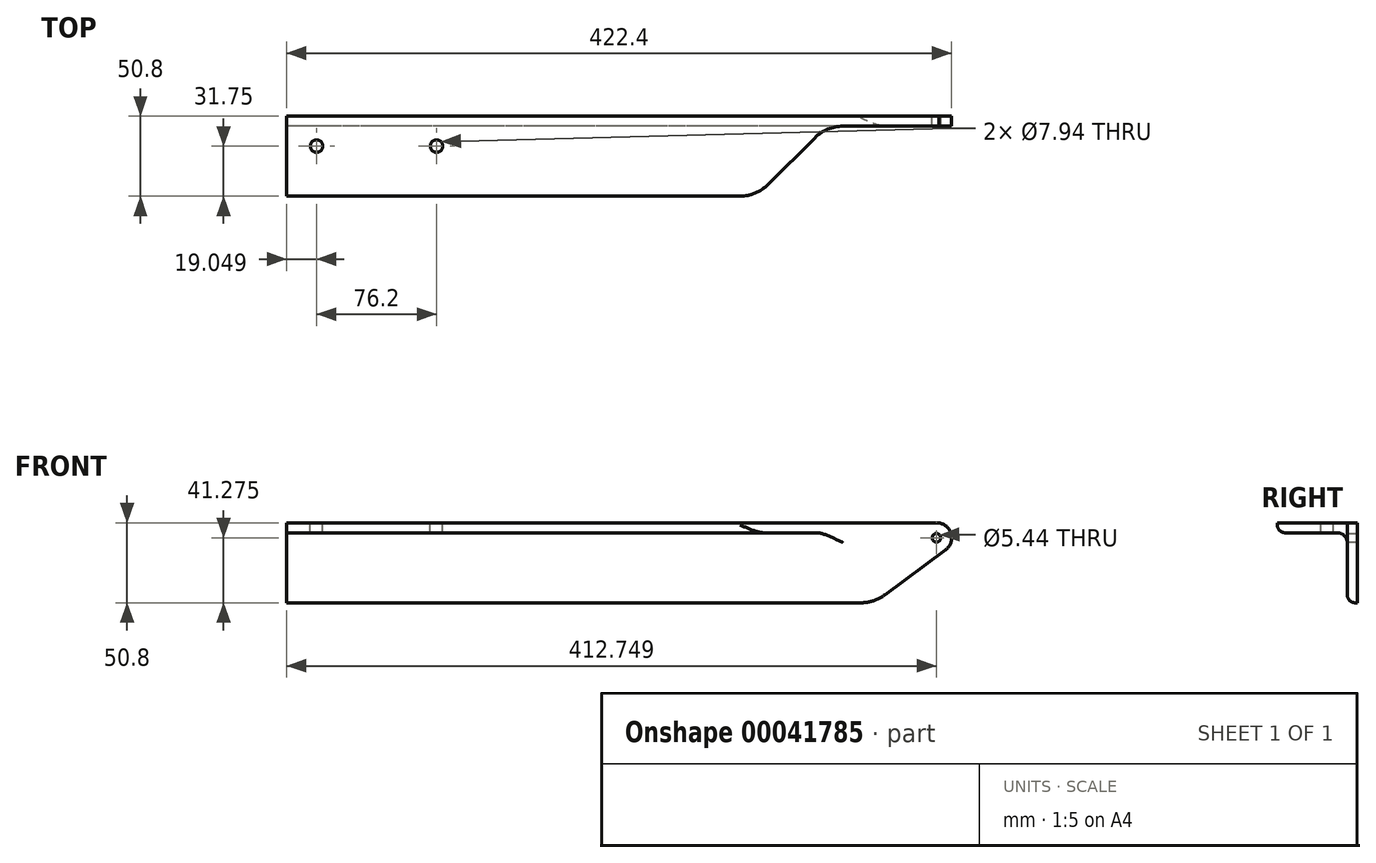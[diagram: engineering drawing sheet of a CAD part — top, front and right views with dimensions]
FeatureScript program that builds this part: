
annotation { "Feature Type Name" : "Feature", "Feature Type Description" : "" }
export const myFeature = defineFeature(function(context is Context, id is Id, definition is map)
    precondition{}
    {
        {
            var Q0;
            Q0=qCreatedBy(makeId("Right.planeOp"),FACE);
            var sketch = newSketch(context, id + "F0", { "sketchPlane" : qUnion([Q0])});
            skLineSegment(sketch, "E0.bottom", {"start": v(0, 0) * mm, "end": v(50.8, 0) * mm});
            skLineSegment(sketch, "E0.top", {"start": v(0, -50.8) * mm, "end": v(1.27, -50.8) * mm});
            skLineSegment(sketch, "E0.left", {"start": v(0, 0) * mm, "end": v(0, -50.8) * mm});
            skLineSegment(sketch, "E0.right", {"start": v(50.8, 0) * mm, "end": v(50.8, -1.27) * mm});
            skLineSegment(sketch, "E1.0", {"start": v(12.7, -6.35) * mm, "end": v(45.72, -6.35) * mm});
            skLineSegment(sketch, "E1.1", {"start": v(6.35, -12.7) * mm, "end": v(6.35, -45.72) * mm});
            skPoint(sketch, "E2.visualSharp", {"position": v(50.8, -6.35) * mm});
            skArc(sketch, "E2.filletArc", {"start": v(45.72, -6.35) * mm, "mid": v(49.31, -4.86) * mm, "end": v(50.8, -1.27) * mm});
            skPoint(sketch, "E3.visualSharp", {"position": v(6.35, -50.8) * mm});
            skArc(sketch, "E3.filletArc", {"start": v(1.27, -50.8) * mm, "mid": v(4.86, -49.31) * mm, "end": v(6.35, -45.72) * mm});
            skPoint(sketch, "E4.visualSharp", {"position": v(6.35, -6.35) * mm});
            skArc(sketch, "E4.filletArc", {"start": v(12.7, -6.35) * mm, "mid": v(8.2, -8.2) * mm, "end": v(6.35, -12.7) * mm});
            skSolve(sketch);
        }
        {
            var Q0;
            Q0=qSketchRegion(id+"F0",true);
            extrude(context, id + "F1", {"entities" : qUnion([Q0]), "endBound" : BoundingType.SYMMETRIC, "depth" : 422.4 * mm});
        }
        {
            var Q0;
            Q0=makeQuery(id+"F1.opExtrude","SWEPT_FACE",FACE,{"disambiguationData":[OSD([sQuery(id+"F0.wireOp",EDGE,"E0.bottom")])]});
            var sketch = newSketch(context, id + "F2", { "sketchPlane" : qUnion([Q0])});
            skLineSegment(sketch, "E5.0", {"start": v(211.2, 19.05) * mm, "end": v(-211.2, 19.05) * mm, "construction": true});
            skLineSegment(sketch, "E6.0", {"start": v(-192.15, 0) * mm, "end": v(-192.15, 50.8) * mm, "construction": true});
            skLineSegment(sketch, "E7.0", {"start": v(-115.95, 0) * mm, "end": v(-115.95, 50.8) * mm, "construction": true});
            skCircle(sketch, "E8", {"center": v(-192.15, 19.05) * mm, "radius": 3.97 * mm});
            skCircle(sketch, "E9", {"center": v(-115.95, 19.05) * mm, "radius": 3.97 * mm});
            skSolve(sketch);
        }
        {
            var Q0;
            Q0=qSketchRegion(id+"F2",true);
            extrude(context, id + "F3", {"entities" : qUnion([Q0]), "operationType" : NewBodyOperationType.REMOVE, "oppositeDirection" : true, "depth" : 25.4 * mm});
        }
        {
            var Q0;
            Q0=makeQuery(id+"F1.opExtrude","SWEPT_FACE",FACE,{"disambiguationData":[OSD([sQuery(id+"F0.wireOp",EDGE,"E0.bottom")])]});
            var sketch = newSketch(context, id + "F4", { "sketchPlane" : qUnion([Q0])});
            skLineSegment(sketch, "E10.0", {"start": v(211.2, 6.35) * mm, "end": v(-211.2, 6.35) * mm, "construction": true});
            skLineSegment(sketch, "E11.0", {"start": v(-211.2, 0) * mm, "end": v(-211.2, 50.8) * mm, "construction": true});
            skLineSegment(sketch, "E12.0", {"start": v(87.25, 0) * mm, "end": v(87.25, 50.8) * mm, "construction": true});
            skLineSegment(sketch, "E13.0", {"start": v(131.7, 0) * mm, "end": v(131.7, 50.8) * mm, "construction": true});
            skLineSegment(sketch, "E14.0", {"start": v(211.2, 0) * mm, "end": v(211.2, 50.8) * mm, "construction": true});
            skLineSegment(sketch, "E15.0", {"start": v(211.2, 50.8) * mm, "end": v(-211.2, 50.8) * mm, "construction": true});
            skLineSegment(sketch, "E16", {"start": v(211.2, 6.35) * mm, "end": v(211.2, 50.8) * mm});
            skLineSegment(sketch, "E17", {"start": v(87.25, 50.8) * mm, "end": v(211.2, 50.8) * mm});
            skLineSegment(sketch, "E18", {"start": v(87.25, 50.8) * mm, "end": v(131.7, 6.35) * mm});
            skLineSegment(sketch, "E19", {"start": v(131.7, 6.35) * mm, "end": v(211.2, 6.35) * mm});
            skSolve(sketch);
        }
        {
            var Q0;
            Q0=qSketchRegion(id+"F4",true);
            extrude(context, id + "F5", {"entities" : qUnion([Q0]), "operationType" : NewBodyOperationType.REMOVE, "endBound" : BoundingType.THROUGH_ALL, "oppositeDirection" : true, "depth" : 25.4 * mm});
        }
        {
            var Q0;
            Q0=makeQuery(id+"F5.boolean.opBoolean","COPY",EDGE,{"derivedFrom":makeQuery(id+"F5.opExtrude","SWEPT_EDGE",EDGE,{"disambiguationData":[OSD([sQuery(id+"F4.wireOp",EDGE,"E18"),sQuery(id+"F4.wireOp",EDGE,"E19")])]})});
            fillet(context, id + "F6", {"entities" : qUnion([Q0]), "radius" : 25.4 * mm, "tangentPropagation" : true, "allowEdgeOverflow" : false});
        }
        {
            var Q0;
            Q0=makeQuery(id+"F1.opExtrude","SWEPT_FACE",FACE,{"disambiguationData":[OSD([sQuery(id+"F0.wireOp",EDGE,"E0.bottom")])]});
            var sketch = newSketch(context, id + "F7", { "sketchPlane" : qUnion([Q0])});
            skLineSegment(sketch, "E20.0", {"start": v(94.69, 43.36) * mm, "end": v(124.26, 13.79) * mm});
            skLineSegment(sketch, "E21.0", {"start": v(76.73, 50.8) * mm, "end": v(-211.2, 50.8) * mm});
            skPoint(sketch, "E22.visualSharp", {"position": v(87.25, 50.8) * mm});
            skArc(sketch, "E22.filletArc", {"start": v(94.69, 43.36) * mm, "mid": v(86.45, 48.87) * mm, "end": v(76.73, 50.8) * mm});
            skLineSegment(sketch, "E23", {"start": v(76.73, 50.8) * mm, "end": v(76.73, 68.3) * mm});
            skLineSegment(sketch, "E24", {"start": v(76.73, 68.3) * mm, "end": v(108.3, 68.3) * mm});
            skLineSegment(sketch, "E25", {"start": v(108.3, 68.3) * mm, "end": v(108.3, 43.36) * mm});
            skLineSegment(sketch, "E26", {"start": v(108.3, 43.36) * mm, "end": v(94.69, 43.36) * mm});
            skSolve(sketch);
        }
        {
            var Q0;
            Q0=qSketchRegion(id+"F7",true);
            extrude(context, id + "F8", {"entities" : qUnion([Q0]), "operationType" : NewBodyOperationType.REMOVE, "endBound" : BoundingType.THROUGH_ALL, "oppositeDirection" : true, "depth" : 25.4 * mm});
        }
        {
            var Q0;
            Q0=makeQuery(id+"F1.opExtrude","SWEPT_FACE",FACE,{"disambiguationData":[OSD([sQuery(id+"F0.wireOp",EDGE,"E0.left")])]});
            var sketch = newSketch(context, id + "F9", { "sketchPlane" : qUnion([Q0])});
            skLineSegment(sketch, "E27.0", {"start": v(-211.2, 0) * mm, "end": v(-211.2, -50.8) * mm, "construction": true});
            skLineSegment(sketch, "E28.0", {"start": v(201.55, 0) * mm, "end": v(201.55, -50.8) * mm, "construction": true});
            skLineSegment(sketch, "E29.0", {"start": v(161.93, 0) * mm, "end": v(161.93, -50.8) * mm, "construction": true});
            skLineSegment(sketch, "E30.0", {"start": v(211.2, -50.8) * mm, "end": v(-211.2, -50.8) * mm});
            skLineSegment(sketch, "E31.0", {"start": v(211.2, 0) * mm, "end": v(-211.2, 0) * mm, "construction": true});
            skLineSegment(sketch, "E32.0", {"start": v(211.2, -9.53) * mm, "end": v(-211.2, -9.53) * mm, "construction": true});
            skCircle(sketch, "E33", {"center": v(201.55, -9.52) * mm, "radius": 2.72 * mm});
            skArc(sketch, "E34", {"start": v(207.28, -17.29) * mm, "mid": v(210.72, -6.5) * mm, "end": v(201.55, 0.13) * mm});
            skLineSegment(sketch, "E35", {"start": v(161.93, -50.8) * mm, "end": v(207.28, -17.29) * mm});
            skLineSegment(sketch, "E36", {"start": v(201.55, 0) * mm, "end": v(201.55, 11.9) * mm});
            skLineSegment(sketch, "E37", {"start": v(161.93, -50.8) * mm, "end": v(161.93, -62.77) * mm});
            skLineSegment(sketch, "E38", {"start": v(201.55, 11.9) * mm, "end": v(237.1, 11.9) * mm});
            skLineSegment(sketch, "E39", {"start": v(161.93, -62.77) * mm, "end": v(237.1, -62.77) * mm});
            skLineSegment(sketch, "E40", {"start": v(237.1, -62.77) * mm, "end": v(237.1, 11.9) * mm});
            skSolve(sketch);
        }
        {
            var Q0;
            Q0=qSketchRegion(id+"F9",true);
            extrude(context, id + "F10", {"entities" : qUnion([Q0]), "operationType" : NewBodyOperationType.REMOVE, "endBound" : BoundingType.THROUGH_ALL, "oppositeDirection" : true, "depth" : 25.4 * mm});
        }
        {
            var Q0;
            Q0=makeQuery(id+"F1.opExtrude","SWEPT_FACE",FACE,{"disambiguationData":[OSD([sQuery(id+"F0.wireOp",EDGE,"E0.left")])]});
            var sketch = newSketch(context, id + "F11", { "sketchPlane" : qUnion([Q0])});
            skLineSegment(sketch, "E41.0", {"start": v(168.65, -45.83) * mm, "end": v(207.28, -17.29) * mm});
            skLineSegment(sketch, "E42.0", {"start": v(153.56, -50.8) * mm, "end": v(-211.2, -50.8) * mm});
            skPoint(sketch, "E43.visualSharp", {"position": v(161.93, -50.8) * mm});
            skArc(sketch, "E43.filletArc", {"start": v(153.56, -50.8) * mm, "mid": v(161.5, -49.53) * mm, "end": v(168.65, -45.83) * mm});
            skLineSegment(sketch, "E44", {"start": v(153.56, -50.8) * mm, "end": v(153.56, -83.13) * mm});
            skLineSegment(sketch, "E45", {"start": v(207.28, -17.29) * mm, "end": v(207.28, -83.13) * mm});
            skLineSegment(sketch, "E46", {"start": v(207.28, -83.13) * mm, "end": v(153.56, -83.13) * mm});
            skSolve(sketch);
        }
        {
            var Q0;
            Q0=qSketchRegion(id+"F11",true);
            extrude(context, id + "F12", {"entities" : qUnion([Q0]), "operationType" : NewBodyOperationType.REMOVE, "endBound" : BoundingType.THROUGH_ALL, "oppositeDirection" : true, "depth" : 25.4 * mm});
        }
        {
            var Q0;
            Q0=makeQuery(id+"F1.opExtrude","SWEPT_BODY",BODY,{"disambiguationData":[OSD([sQuery(id+"F0.wireOp",EDGE,"E0.bottom"),sQuery(id+"F0.wireOp",EDGE,"E0.top"),sQuery(id+"F0.wireOp",EDGE,"E0.left"),sQuery(id+"F0.wireOp",EDGE,"E0.right"),sQuery(id+"F0.wireOp",EDGE,"E1.0"),sQuery(id+"F0.wireOp",EDGE,"E1.1"),sQuery(id+"F0.wireOp",EDGE,"E2.filletArc"),sQuery(id+"F0.wireOp",EDGE,"E3.filletArc"),sQuery(id+"F0.wireOp",EDGE,"E4.filletArc")])]});
            var Q1;
            Q1=qCreatedBy(makeId("Front.planeOp"),FACE);
            mirror(context, id + "F13", {"entities" : qUnion([Q0]), "mirrorPlane" : qUnion([Q1])});
        }
        {
            var Q0;
            Q0=makeQuery(id+"F1.opExtrude","SWEPT_BODY",BODY,{"disambiguationData":[OSD([sQuery(id+"F0.wireOp",EDGE,"E0.bottom"),sQuery(id+"F0.wireOp",EDGE,"E0.top"),sQuery(id+"F0.wireOp",EDGE,"E0.left"),sQuery(id+"F0.wireOp",EDGE,"E0.right"),sQuery(id+"F0.wireOp",EDGE,"E1.0"),sQuery(id+"F0.wireOp",EDGE,"E1.1"),sQuery(id+"F0.wireOp",EDGE,"E2.filletArc"),sQuery(id+"F0.wireOp",EDGE,"E3.filletArc"),sQuery(id+"F0.wireOp",EDGE,"E4.filletArc")])]});
            deleteBodies(context, id + "F14", {"entities" : qUnion([Q0])});
        }
    });
